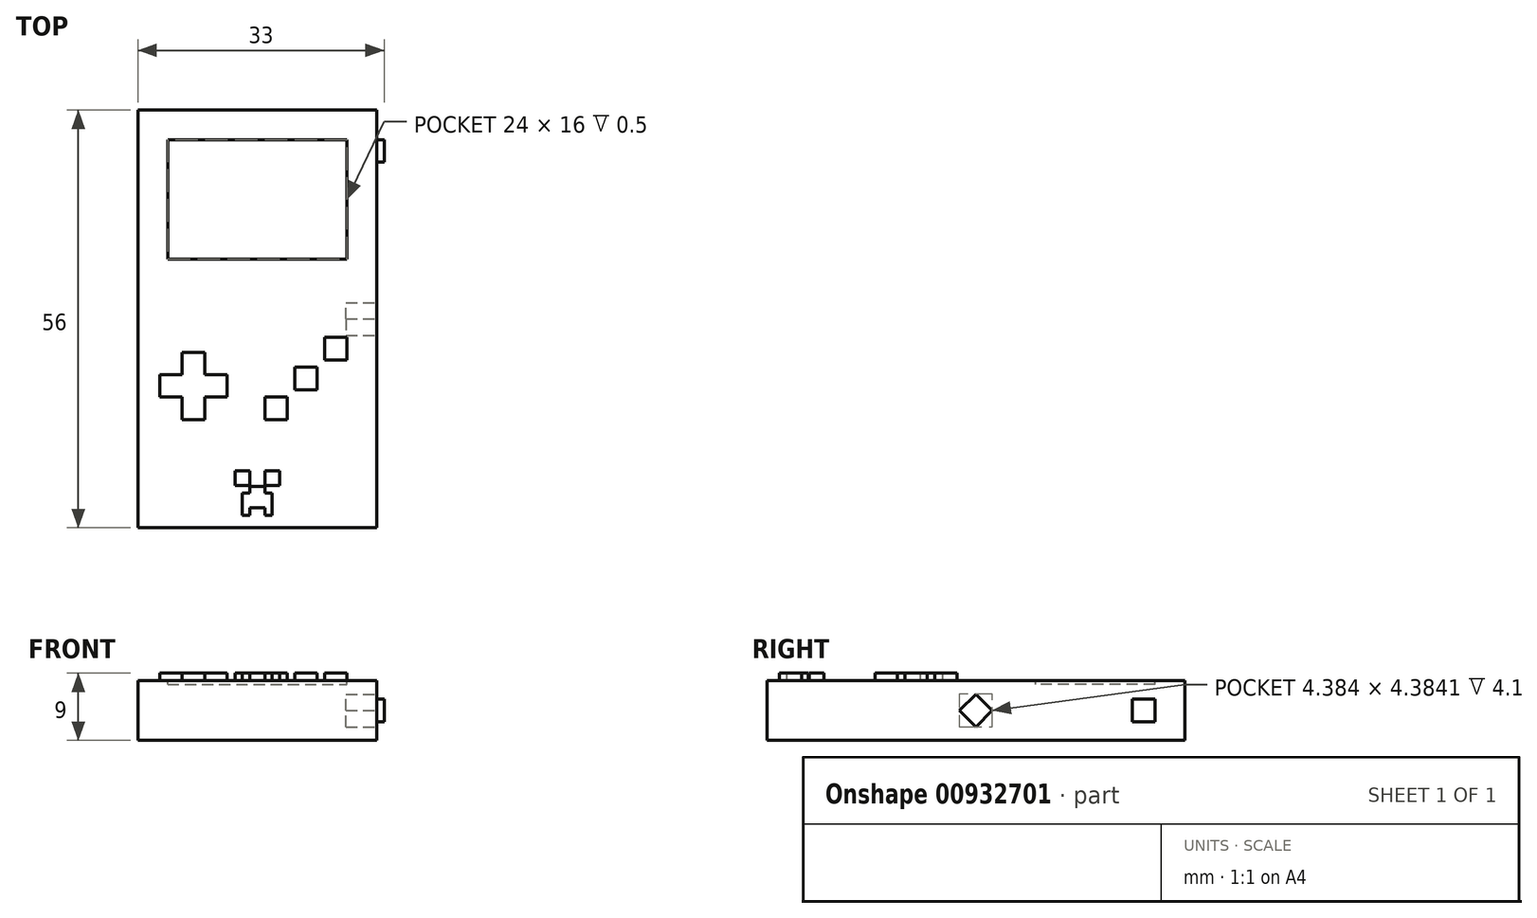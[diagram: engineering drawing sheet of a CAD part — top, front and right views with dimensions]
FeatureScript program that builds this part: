
annotation { "Feature Type Name" : "Feature", "Feature Type Description" : "" }
export const myFeature = defineFeature(function(context is Context, id is Id, definition is map)
    precondition{}
    {
        {
            var Q0;
            Q0=qCreatedBy(makeId("Top.planeOp"),FACE);
            var sketch = newSketch(context, id + "F0", { "sketchPlane" : qUnion([Q0])});
            skLineSegment(sketch, "E0.bottom", {"start": v(-16, 28) * mm, "end": v(16, 28) * mm});
            skLineSegment(sketch, "E0.top", {"start": v(-16, -28) * mm, "end": v(16, -28) * mm});
            skLineSegment(sketch, "E0.left", {"start": v(-16, 28) * mm, "end": v(-16, -28) * mm});
            skLineSegment(sketch, "E0.right", {"start": v(16, 28) * mm, "end": v(16, -28) * mm});
            skSolve(sketch);
        }
        {
            var Q0;
            Q0 = qSketchRegion(id + "F0", true);
            extrude(context, id + "F1", {"entities" : qUnion([Q0]), "depth" : 8 * mm, "offsetDistance" : 25 * mm});
        }
        {
            var Q0;
            Q0=makeQuery(id+"F1.opExtrude","SWEPT_FACE",FACE,{"disambiguationData":[OSD([sQuery(id+"F0.wireOp",EDGE,"E0.right")])]});
            var sketch = newSketch(context, id + "F2", { "sketchPlane" : qUnion([Q0])});
            skLineSegment(sketch, "E1.bottom", {"start": v(24, 5.5) * mm, "end": v(21, 5.5) * mm});
            skLineSegment(sketch, "E1.top", {"start": v(24, 2.5) * mm, "end": v(21, 2.5) * mm});
            skLineSegment(sketch, "E1.left", {"start": v(24, 5.5) * mm, "end": v(24, 2.5) * mm});
            skLineSegment(sketch, "E1.right", {"start": v(21, 5.5) * mm, "end": v(21, 2.5) * mm});
            skSolve(sketch);
        }
        {
            var Q0;
            Q0 = qSketchRegion(id + "F2", true);
            extrude(context, id + "F3", {"entities" : qUnion([Q0]), "operationType" : NewBodyOperationType.ADD, "depth" : 1 * mm, "offsetDistance" : 25 * mm});
        }
        {
            var Q0;
            Q0=makeQuery(id+"F1.opExtrude","CAP_FACE",FACE,{"disambiguationData":[OSD([sQuery(id+"F0.wireOp",EDGE,"E0.bottom"),sQuery(id+"F0.wireOp",EDGE,"E0.top"),sQuery(id+"F0.wireOp",EDGE,"E0.left"),sQuery(id+"F0.wireOp",EDGE,"E0.right")])],"isStart":false});
            var sketch = newSketch(context, id + "F4", { "sketchPlane" : qUnion([Q0])});
            skLineSegment(sketch, "E2.bottom", {"start": v(-12, 24) * mm, "end": v(12, 24) * mm});
            skLineSegment(sketch, "E2.top", {"start": v(-12, 8) * mm, "end": v(12, 8) * mm});
            skLineSegment(sketch, "E2.left", {"start": v(-12, 24) * mm, "end": v(-12, 8) * mm});
            skLineSegment(sketch, "E2.right", {"start": v(12, 24) * mm, "end": v(12, 8) * mm});
            skLineSegment(sketch, "E3", {"start": v(16, -4) * mm, "end": v(-16, -4) * mm, "construction": true});
            skLineSegment(sketch, "E4.bottom", {"start": v(9, -2.5) * mm, "end": v(12, -2.5) * mm});
            skLineSegment(sketch, "E4.top", {"start": v(9, -5.5) * mm, "end": v(12, -5.5) * mm});
            skLineSegment(sketch, "E4.left", {"start": v(9, -2.5) * mm, "end": v(9, -5.5) * mm});
            skLineSegment(sketch, "E4.right", {"start": v(12, -2.5) * mm, "end": v(12, -5.5) * mm});
            skLineSegment(sketch, "E5.bottom", {"start": v(1, -10.5) * mm, "end": v(4, -10.5) * mm});
            skLineSegment(sketch, "E5.top", {"start": v(1, -13.5) * mm, "end": v(4, -13.5) * mm});
            skLineSegment(sketch, "E5.left", {"start": v(1, -10.5) * mm, "end": v(1, -13.5) * mm});
            skLineSegment(sketch, "E5.right", {"start": v(4, -10.5) * mm, "end": v(4, -13.5) * mm});
            skLineSegment(sketch, "E6.bottom", {"start": v(5, -6.5) * mm, "end": v(8, -6.5) * mm});
            skLineSegment(sketch, "E6.top", {"start": v(5, -9.5) * mm, "end": v(8, -9.5) * mm});
            skLineSegment(sketch, "E6.left", {"start": v(5, -6.5) * mm, "end": v(5, -9.5) * mm});
            skLineSegment(sketch, "E6.right", {"start": v(8, -6.5) * mm, "end": v(8, -9.5) * mm});
            skLineSegment(sketch, "E7.bottom", {"start": v(-13.05, -7.5) * mm, "end": v(-10.05, -7.5) * mm});
            skLineSegment(sketch, "E7.top", {"start": v(-13.05, -10.5) * mm, "end": v(-10.05, -10.5) * mm});
            skLineSegment(sketch, "E7.left", {"start": v(-13.05, -7.5) * mm, "end": v(-13.05, -10.5) * mm});
            skLineSegment(sketch, "E7.right", {"start": v(-4.05, -7.5) * mm, "end": v(-4.05, -10.5) * mm});
            skLineSegment(sketch, "E8.bottom", {"start": v(-10.05, -4.5) * mm, "end": v(-7.05, -4.5) * mm});
            skLineSegment(sketch, "E8.top", {"start": v(-10.05, -13.5) * mm, "end": v(-7.05, -13.5) * mm});
            skLineSegment(sketch, "E8.left", {"start": v(-10.05, -4.5) * mm, "end": v(-10.05, -7.5) * mm});
            skLineSegment(sketch, "E8.right", {"start": v(-7.05, -4.5) * mm, "end": v(-7.05, -7.5) * mm});
            skLineSegment(sketch, "E9.trimOffspring", {"start": v(-7.05, -7.5) * mm, "end": v(-4.05, -7.5) * mm});
            skLineSegment(sketch, "E10.trimOffspring", {"start": v(-10.05, -10.5) * mm, "end": v(-10.05, -13.5) * mm});
            skLineSegment(sketch, "E11.trimOffspring", {"start": v(-7.05, -10.5) * mm, "end": v(-4.05, -10.5) * mm});
            skLineSegment(sketch, "E12.trimOffspring", {"start": v(-7.05, -10.5) * mm, "end": v(-7.05, -13.5) * mm});
            skLineSegment(sketch, "E13.bottom", {"start": v(-3, -20.36) * mm, "end": v(-1, -20.36) * mm});
            skLineSegment(sketch, "E13.top", {"start": v(-3, -22.36) * mm, "end": v(-1, -22.36) * mm});
            skLineSegment(sketch, "E13.left", {"start": v(-3, -20.36) * mm, "end": v(-3, -22.36) * mm});
            skLineSegment(sketch, "E13.right", {"start": v(-1, -20.36) * mm, "end": v(-1, -22.36) * mm});
            skLineSegment(sketch, "E14", {"start": v(-2, -23.36) * mm, "end": v(-2, -26.36) * mm});
            skLineSegment(sketch, "E15", {"start": v(-2, -26.36) * mm, "end": v(-1, -26.36) * mm});
            skLineSegment(sketch, "E16", {"start": v(-1, -26.36) * mm, "end": v(-1, -25.36) * mm});
            skLineSegment(sketch, "E17", {"start": v(-1, -25.36) * mm, "end": v(0, -25.36) * mm});
            skLineSegment(sketch, "E18", {"start": v(-2, -23.36) * mm, "end": v(-1, -23.36) * mm});
            skLineSegment(sketch, "E19.MirrorCS", {"start": v(2, -26.36) * mm, "end": v(1, -26.36) * mm});
            skLineSegment(sketch, "E20.MirrorCS", {"start": v(3, -20.36) * mm, "end": v(1, -20.36) * mm});
            skLineSegment(sketch, "E21.MirrorCS", {"start": v(3, -20.36) * mm, "end": v(3, -22.36) * mm});
            skLineSegment(sketch, "E22.MirrorCS", {"start": v(2, -23.36) * mm, "end": v(1, -23.36) * mm});
            skLineSegment(sketch, "E23.MirrorCS", {"start": v(1, -25.36) * mm, "end": v(0, -25.36) * mm});
            skLineSegment(sketch, "E24.MirrorCS", {"start": v(1, -20.36) * mm, "end": v(1, -22.36) * mm});
            skLineSegment(sketch, "E25.MirrorCS", {"start": v(3, -22.36) * mm, "end": v(1, -22.36) * mm});
            skLineSegment(sketch, "E26.MirrorCS", {"start": v(1, -26.36) * mm, "end": v(1, -25.36) * mm});
            skLineSegment(sketch, "E27.MirrorCS", {"start": v(2, -23.36) * mm, "end": v(2, -26.36) * mm});
            skLineSegment(sketch, "E28", {"start": v(-1, -23.36) * mm, "end": v(-1, -22.46) * mm});
            skLineSegment(sketch, "E29", {"start": v(-1, -22.46) * mm, "end": v(1, -22.46) * mm});
            skLineSegment(sketch, "E30", {"start": v(1, -22.46) * mm, "end": v(1, -23.36) * mm});
            skSolve(sketch);
        }
        {
            var Q0;
            Q0=makeQuery(id+"F4.imprint","IMPRINT",FACE,{"disambiguationData":[TD([[makeQuery(id+"F4.imprint","IMPRINT",EDGE,{"derivedFrom":sQuery(id+"F4.wireOp",EDGE,"E2.bottom")}),-1.0]])]});
            extrude(context, id + "F5", {"entities" : qUnion([Q0]), "operationType" : NewBodyOperationType.REMOVE, "oppositeDirection" : true, "depth" : 0.5 * mm, "offsetDistance" : 25 * mm});
        }
        {
            var Q0;
            Q0=makeQuery(id+"F4.imprint","IMPRINT",FACE,{"disambiguationData":[TD([[makeQuery(id+"F4.imprint","IMPRINT",EDGE,{"derivedFrom":sQuery(id+"F4.wireOp",EDGE,"E7.bottom")}),-1.0]])]});
            var Q1;
            Q1=makeQuery(id+"F4.imprint","IMPRINT",FACE,{"disambiguationData":[TD([[makeQuery(id+"F4.imprint","IMPRINT",EDGE,{"derivedFrom":sQuery(id+"F4.wireOp",EDGE,"E5.bottom")}),-1.0]])]});
            var Q2;
            Q2=makeQuery(id+"F4.imprint","IMPRINT",FACE,{"disambiguationData":[TD([[makeQuery(id+"F4.imprint","IMPRINT",EDGE,{"derivedFrom":sQuery(id+"F4.wireOp",EDGE,"E6.bottom")}),-1.0]])]});
            var Q3;
            Q3=makeQuery(id+"F4.imprint","IMPRINT",FACE,{"disambiguationData":[TD([[makeQuery(id+"F4.imprint","IMPRINT",EDGE,{"derivedFrom":sQuery(id+"F4.wireOp",EDGE,"E4.bottom")}),-1.0]])]});
            var Q4;
            Q4=makeQuery(id+"F4.imprint","IMPRINT",FACE,{"disambiguationData":[TD([[makeQuery(id+"F4.imprint","IMPRINT",EDGE,{"derivedFrom":sQuery(id+"F4.wireOp",EDGE,"E13.bottom")}),-1.0]])]});
            var Q5;
            Q5=makeQuery(id+"F4.imprint","IMPRINT",FACE,{"disambiguationData":[TD([[makeQuery(id+"F4.imprint","IMPRINT",EDGE,{"derivedFrom":sQuery(id+"F4.wireOp",EDGE,"E20.MirrorCS")}),1.0]])]});
            var Q6;
            Q6=makeQuery(id+"F4.imprint","IMPRINT",FACE,{"disambiguationData":[TD([[makeQuery(id+"F4.imprint","IMPRINT",EDGE,{"derivedFrom":sQuery(id+"F4.wireOp",EDGE,"E14")}),1.0]])]});
            extrude(context, id + "F6", {"entities" : qUnion([Q0, Q1, Q2, Q3, Q4, Q5, Q6]), "operationType" : NewBodyOperationType.ADD, "depth" : 1 * mm, "offsetDistance" : 25 * mm});
        }
        {
            var Q0;
            Q0=makeQuery(id+"F1.opExtrude","SWEPT_FACE",FACE,{"disambiguationData":[OSD([sQuery(id+"F0.wireOp",EDGE,"E0.right")])]});
            var sketch = newSketch(context, id + "F7", { "sketchPlane" : qUnion([Q0])});
            skLineSegment(sketch, "E31", {"start": v(2.2, 4) * mm, "end": v(0, 6.18) * mm});
            skLineSegment(sketch, "E32", {"start": v(0, 6.18) * mm, "end": v(-2.2, 4) * mm});
            skLineSegment(sketch, "E33", {"start": v(-2.2, 4) * mm, "end": v(0, 1.8) * mm});
            skLineSegment(sketch, "E34", {"start": v(0, 1.8) * mm, "end": v(2.2, 4) * mm});
            skSolve(sketch);
        }
        {
            var Q0;
            Q0 = qSketchRegion(id + "F7", true);
            extrude(context, id + "F8", {"entities" : qUnion([Q0]), "operationType" : NewBodyOperationType.REMOVE, "oppositeDirection" : true, "depth" : 4.1 * mm, "offsetDistance" : 25 * mm});
        }
    });
